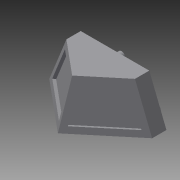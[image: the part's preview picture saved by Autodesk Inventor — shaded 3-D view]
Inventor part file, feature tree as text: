
AUTODESK INVENTOR PART (.ipt)
format: ipt  version: 2015 (Build 190159000, 159)  size: 147,968 bytes
history: native  units: in
note: dims shown in document units (in); Inventor stores cm internally (conversion verified against a paired STEP export)
features: sketch x5, extrude x3, plane x1, loft x1, shell x1, chamfer x1
ambient origin geometry x8: Origin, YZ Plane, XZ Plane, XY Plane, X Axis, Y Axis, Z Axis, Center Point
bodies: Body1 (feature_tree)
feature tree (12):
  sketch  "Sketch1"  dims[d0=0.25in d1=0.25in d2=1.8in]
  plane  "Work Plane2"
  loft  "Loft1"
  shell  "Shell1"  Thickness=1.8in
  extrude  "Extrusion2"  Depth=0.9in
  extrude  "Extrusion3"  Depth=0.25in
  extrude  "Extrusion4"  Depth=0.6in
  chamfer  "Chamfer1"  Distance=1.2in
  sketch  "Sketch2"  dims[d3=0.9in d4=0.9in]
  sketch  "Sketch4"  dims[d5=1.0in d8=0.25in]
  sketch  "Sketch5"  dims[d9=0.25in d10=0.6in]
  sketch  "Sketch6"  dims[d11=0.6in d12=1.2in d15=0.0in d16=0.0in d17=90.0deg d18=0.0in d19=90.0deg d20=0.1in d21=0.1in d22=0.1in d23=0.1in d24=0.1in d25=0.05in d26=0.0in d27=0.1in d29=0.1in d32=0.1in d34=0.1in d35=0.05in d36=0.0in d37=0.275in d38=0.275in d39=0.125in d40=0.125in d41=0.125in d42=0.9in d43=0.125in d44=0.125in d45=0.125in d46=0.125in d47=0.0in d48=0.01in d49=0.125in d50=45.0deg]
